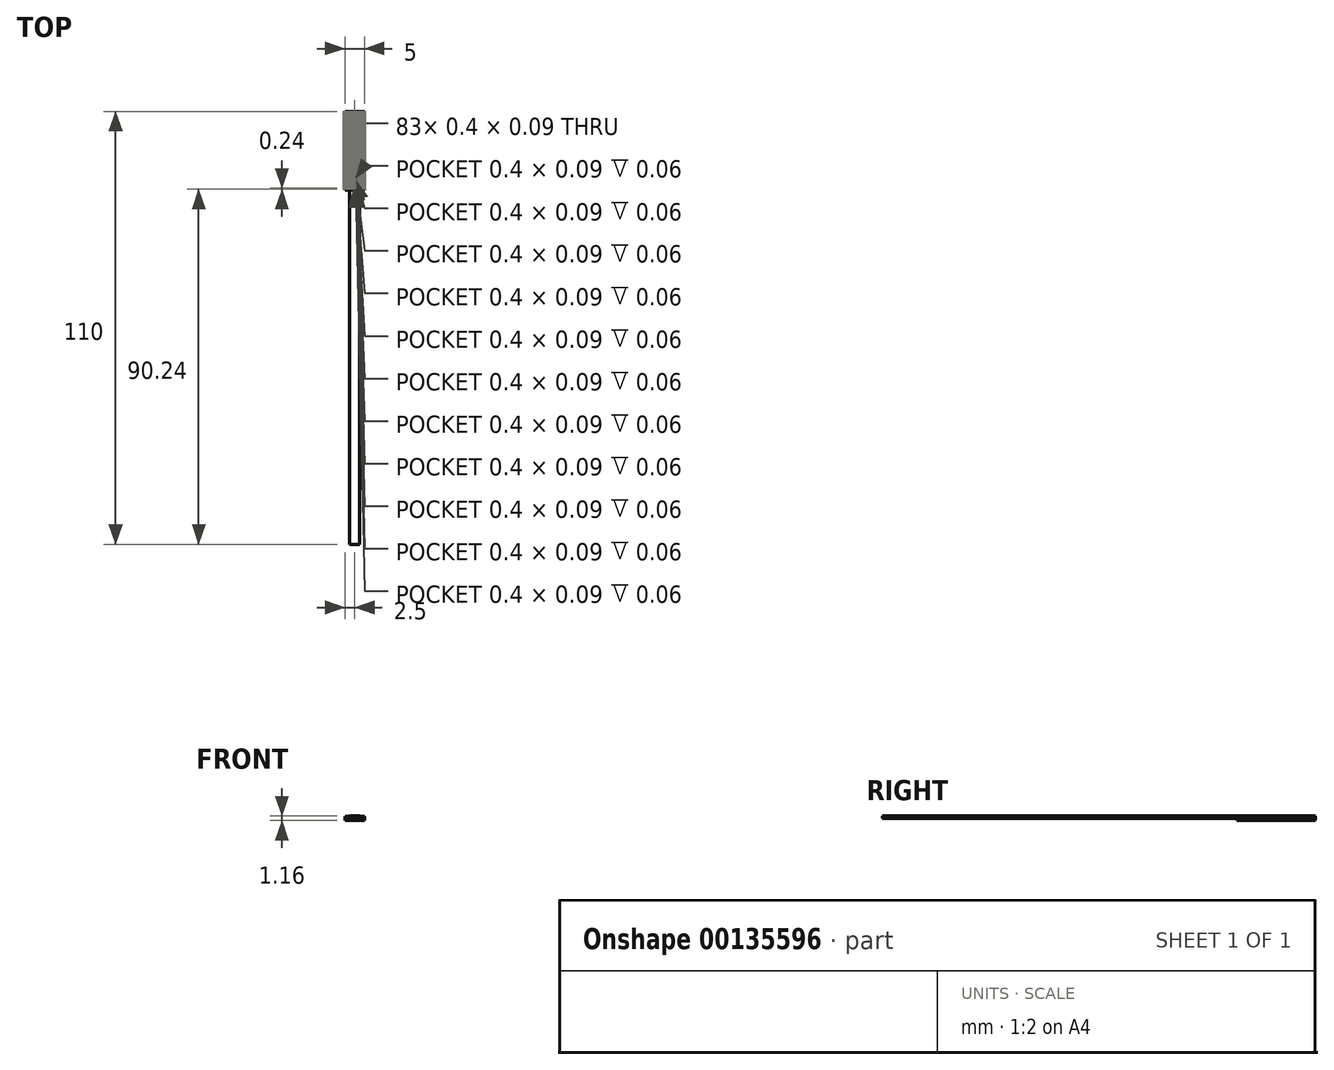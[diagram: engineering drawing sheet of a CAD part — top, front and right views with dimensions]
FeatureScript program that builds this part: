
annotation { "Feature Type Name" : "Feature", "Feature Type Description" : "" }
export const myFeature = defineFeature(function(context is Context, id is Id, definition is map)
    precondition{}
    {
        {
            assignVariable(context, id + "F0", {"name" : "Lz", "anyValue" : 20 * mm});
        }
        {
            var Q0;
            Q0=qCreatedBy(makeId("Top.planeOp"),FACE);
            var sketch = newSketch(context, id + "F1", { "sketchPlane" : qUnion([Q0])});
            skLineSegment(sketch, "E0.bottom", {"start": v(1.25, 10) * mm, "end": v(-1.25, 10) * mm});
            skLineSegment(sketch, "E0.top", {"start": v(1.25, -10) * mm, "end": v(-1.25, -10) * mm});
            skLineSegment(sketch, "E0.left", {"start": v(1.25, 10) * mm, "end": v(1.25, -10) * mm});
            skLineSegment(sketch, "E0.right", {"start": v(-1.25, 10) * mm, "end": v(-1.25, -10) * mm});
            skPoint(sketch, "E0.middle", {"position": v(0, 0) * mm});
            skLineSegment(sketch, "E1.bottom", {"start": v(2.5, 10) * mm, "end": v(-2.5, 10) * mm});
            skLineSegment(sketch, "E1.top", {"start": v(2.5, -10) * mm, "end": v(-2.5, -10) * mm});
            skLineSegment(sketch, "E1.left", {"start": v(2.5, 10) * mm, "end": v(2.5, -10) * mm});
            skLineSegment(sketch, "E1.right", {"start": v(-2.5, 10) * mm, "end": v(-2.5, -10) * mm});
            skSolve(sketch);
        }
        {
            var Q0;
            Q0=qCreatedBy(makeId("Front.planeOp"),FACE);
            var sketch = newSketch(context, id + "F2", { "sketchPlane" : qUnion([Q0])});
            skPoint(sketch, "E2", {"position": v(0.06, -0.1) * mm});
            skEllipse(sketch, "E3", {"center": v(0, -0.17) * mm, "majorRadius": 1.28 * mm, "minorRadius": 0.29 * mm, "majorAxis": v(-1, 0)});
            skSolve(sketch);
        }
        {
            var Q0;
            Q0=makeQuery(id+"F2.imprint","IMPRINT",FACE,{"disambiguationData":[TD([[makeQuery(id+"F2.imprint","IMPRINT",EDGE,{"derivedFrom":sQuery(id+"F2.wireOp",EDGE,"E3")}),1.0]])]});
            extrude(context, id + "F3", {"entities" : qUnion([Q0]), "depth" : 100 * mm, "offsetDistance" : 25 * mm, "hasSecondDirection" : true, "secondDirectionOppositeDirection" : false, "secondDirectionDepth" : getVariable(context, 'Lz') / 2});
        }
        {
            assignVariable(context, id + "F4", {"name" : "tox", "anyValue" : 0.1});
        }
        {
            assignVariable(context, id + "F5", {"name" : "detch", "anyValue" : 0.06});
        }
        {
            assignVariable(context, id + "F6", {"name" : "Hsi", "anyValue" : 0.5});
        }
        {
            var Q0;
            {var subQ0=sQuery(id+"F1.wireOp",EDGE,"E0.right");Q0=makeQuery(id+"F1.imprint","IMPRINT",FACE,{"disambiguationData":[TD([[makeQuery(id+"F1.imprint","IMPRINT",EDGE,{"derivedFrom":subQ0}),-1.0]])]});}
            var Q1;
            {var subQ0=sQuery(id+"F1.wireOp",EDGE,"E0.left");Q1=makeQuery(id+"F1.imprint","IMPRINT",FACE,{"disambiguationData":[TD([[makeQuery(id+"F1.imprint","IMPRINT",EDGE,{"derivedFrom":subQ0}),-1.0]])]});}
            var Q2;
            {var subQ0=sQuery(id+"F1.wireOp",EDGE,"E0.left");Q2=makeQuery(id+"F1.imprint","IMPRINT",FACE,{"disambiguationData":[TD([[makeQuery(id+"F1.imprint","IMPRINT",EDGE,{"derivedFrom":subQ0}),1.0]])]});}
            extrude(context, id + "F7", {"entities" : qUnion([Q0, Q1, Q2]), "oppositeDirection" : true, "depth" : (getVariable(context, 'Hsi') - getVariable(context, 'detch')) * mm});
        }
        {
            var Q0;
            Q0=makeQuery(id+"F7.opExtrude","CAP_FACE",FACE,{"disambiguationData":[OSD([sQuery(id+"F1.wireOp",EDGE,"E1.bottom"),sQuery(id+"F1.wireOp",EDGE,"E1.top"),sQuery(id+"F1.wireOp",EDGE,"E1.left"),sQuery(id+"F1.wireOp",EDGE,"E1.right")])],"isStart":true});
            extrude(context, id + "F8", {"entities" : qUnion([Q0]), "oppositeDirection" : true, "depth" : 1 * mm, "hasSecondDirection" : true, "secondDirectionOppositeDirection" : true, "secondDirectionDepth" : (getVariable(context, 'Hsi') - getVariable(context, 'detch')) * mm});
        }
        {
            var Q0;
            Q0=qCreatedBy(makeId("Top.planeOp"),FACE);
            var sketch = newSketch(context, id + "F9", { "sketchPlane" : qUnion([Q0])});
            skLineSegment(sketch, "E4.bottom", {"start": v(-1.25, 10) * mm, "end": v(1.25, 10) * mm});
            skLineSegment(sketch, "E4.top", {"start": v(-1.25, -10) * mm, "end": v(1.25, -10) * mm});
            skLineSegment(sketch, "E4.left", {"start": v(-1.25, 10) * mm, "end": v(-1.25, -10) * mm});
            skLineSegment(sketch, "E4.right", {"start": v(1.25, 10) * mm, "end": v(1.25, -10) * mm});
            skPoint(sketch, "E4.middle", {"position": v(0, 0) * mm});
            skSolve(sketch);
        }
        {
            var Q0;
            Q0=makeQuery(id+"F9.imprint","IMPRINT",FACE,{"disambiguationData":[TD([[makeQuery(id+"F9.imprint","IMPRINT",EDGE,{"derivedFrom":sQuery(id+"F9.wireOp",EDGE,"E4.bottom")}),-1.0]])]});
            extrude(context, id + "F10", {"entities" : qUnion([Q0]), "operationType" : NewBodyOperationType.ADD, "depth" : (getVariable(context, 'detch')) * mm});
        }
        {
            var Q0;
            Q0=makeQuery(id+"F10.opExtrude","CAP_FACE",FACE,{"disambiguationData":[OSD([sQuery(id+"F9.wireOp",EDGE,"E4.bottom"),sQuery(id+"F9.wireOp",EDGE,"E4.top"),sQuery(id+"F9.wireOp",EDGE,"E4.left"),sQuery(id+"F9.wireOp",EDGE,"E4.right")])],"isStart":false});
            extrude(context, id + "F11", {"entities" : qUnion([Q0]), "depth" : (getVariable(context, 'tox')) * mm});
        }
        {
            var Q0;
            Q0=makeQuery(id+"F11.opExtrude","CAP_FACE",FACE,{"disambiguationData":[OSD([sQuery(id+"F9.wireOp",EDGE,"E4.bottom"),sQuery(id+"F9.wireOp",EDGE,"E4.top"),sQuery(id+"F9.wireOp",EDGE,"E4.left"),sQuery(id+"F9.wireOp",EDGE,"E4.right")])],"isStart":false});
            var sketch = newSketch(context, id + "F12", { "sketchPlane" : qUnion([Q0])});
            skLineSegment(sketch, "E5.bottom", {"start": v(0.2, -9.96) * mm, "end": v(-0.2, -9.96) * mm});
            skLineSegment(sketch, "E5.top", {"start": v(0.2, -10.04) * mm, "end": v(-0.2, -10.04) * mm});
            skLineSegment(sketch, "E5.left", {"start": v(0.2, -9.96) * mm, "end": v(0.2, -10.05) * mm});
            skLineSegment(sketch, "E5.right", {"start": v(-0.2, -9.96) * mm, "end": v(-0.2, -10.05) * mm});
            skPoint(sketch, "E5.middle", {"position": v(0, -10) * mm});
            skLineSegment(sketch, "E6.0.1.0", {"start": v(0.2, -9.72) * mm, "end": v(0.2, -9.8) * mm});
            skLineSegment(sketch, "E6.0.1.1", {"start": v(0.2, -9.8) * mm, "end": v(-0.2, -9.8) * mm});
            skLineSegment(sketch, "E6.0.1.2", {"start": v(-0.2, -9.72) * mm, "end": v(-0.2, -9.8) * mm});
            skLineSegment(sketch, "E6.0.1.3", {"start": v(0.2, -9.72) * mm, "end": v(-0.2, -9.72) * mm});
            skPoint(sketch, "E6.0.1.4", {"position": v(0, -9.76) * mm});
            skLineSegment(sketch, "E6.0.2.0", {"start": v(0.2, -9.48) * mm, "end": v(0.2, -9.57) * mm});
            skLineSegment(sketch, "E6.0.2.1", {"start": v(0.2, -9.56) * mm, "end": v(-0.2, -9.56) * mm});
            skLineSegment(sketch, "E6.0.2.2", {"start": v(-0.2, -9.48) * mm, "end": v(-0.2, -9.57) * mm});
            skLineSegment(sketch, "E6.0.2.3", {"start": v(0.2, -9.48) * mm, "end": v(-0.2, -9.48) * mm});
            skPoint(sketch, "E6.0.2.4", {"position": v(0, -9.52) * mm});
            skLineSegment(sketch, "E6.0.3.0", {"start": v(0.2, -9.24) * mm, "end": v(0.2, -9.33) * mm});
            skLineSegment(sketch, "E6.0.3.1", {"start": v(0.2, -9.32) * mm, "end": v(-0.2, -9.32) * mm});
            skLineSegment(sketch, "E6.0.3.2", {"start": v(-0.2, -9.24) * mm, "end": v(-0.2, -9.33) * mm});
            skLineSegment(sketch, "E6.0.3.3", {"start": v(0.2, -9.24) * mm, "end": v(-0.2, -9.24) * mm});
            skPoint(sketch, "E6.0.3.4", {"position": v(0, -9.28) * mm});
            skLineSegment(sketch, "E6.0.4.0", {"start": v(0.2, -9) * mm, "end": v(0.2, -9.09) * mm});
            skLineSegment(sketch, "E6.0.4.1", {"start": v(0.2, -9.08) * mm, "end": v(-0.2, -9.08) * mm});
            skLineSegment(sketch, "E6.0.4.2", {"start": v(-0.2, -9) * mm, "end": v(-0.2, -9.09) * mm});
            skLineSegment(sketch, "E6.0.4.3", {"start": v(0.2, -9) * mm, "end": v(-0.2, -9) * mm});
            skPoint(sketch, "E6.0.4.4", {"position": v(0, -9.04) * mm});
            skLineSegment(sketch, "E6.0.5.0", {"start": v(0.2, -8.76) * mm, "end": v(0.2, -8.85) * mm});
            skLineSegment(sketch, "E6.0.5.1", {"start": v(0.2, -8.84) * mm, "end": v(-0.2, -8.84) * mm});
            skLineSegment(sketch, "E6.0.5.2", {"start": v(-0.2, -8.76) * mm, "end": v(-0.2, -8.85) * mm});
            skLineSegment(sketch, "E6.0.5.3", {"start": v(0.2, -8.76) * mm, "end": v(-0.2, -8.76) * mm});
            skPoint(sketch, "E6.0.5.4", {"position": v(0, -8.8) * mm});
            skLineSegment(sketch, "E6.0.6.0", {"start": v(0.2, -8.52) * mm, "end": v(0.2, -8.6) * mm});
            skLineSegment(sketch, "E6.0.6.1", {"start": v(0.2, -8.6) * mm, "end": v(-0.2, -8.6) * mm});
            skLineSegment(sketch, "E6.0.6.2", {"start": v(-0.2, -8.52) * mm, "end": v(-0.2, -8.6) * mm});
            skLineSegment(sketch, "E6.0.6.3", {"start": v(0.2, -8.52) * mm, "end": v(-0.2, -8.52) * mm});
            skPoint(sketch, "E6.0.6.4", {"position": v(0, -8.56) * mm});
            skLineSegment(sketch, "E6.0.7.0", {"start": v(0.2, -8.28) * mm, "end": v(0.2, -8.37) * mm});
            skLineSegment(sketch, "E6.0.7.1", {"start": v(0.2, -8.36) * mm, "end": v(-0.2, -8.36) * mm});
            skLineSegment(sketch, "E6.0.7.2", {"start": v(-0.2, -8.28) * mm, "end": v(-0.2, -8.37) * mm});
            skLineSegment(sketch, "E6.0.7.3", {"start": v(0.2, -8.28) * mm, "end": v(-0.2, -8.28) * mm});
            skPoint(sketch, "E6.0.7.4", {"position": v(0, -8.32) * mm});
            skLineSegment(sketch, "E6.0.8.0", {"start": v(0.2, -8.04) * mm, "end": v(0.2, -8.13) * mm});
            skLineSegment(sketch, "E6.0.8.1", {"start": v(0.2, -8.12) * mm, "end": v(-0.2, -8.12) * mm});
            skLineSegment(sketch, "E6.0.8.2", {"start": v(-0.2, -8.04) * mm, "end": v(-0.2, -8.13) * mm});
            skLineSegment(sketch, "E6.0.8.3", {"start": v(0.2, -8.04) * mm, "end": v(-0.2, -8.04) * mm});
            skPoint(sketch, "E6.0.8.4", {"position": v(0, -8.08) * mm});
            skLineSegment(sketch, "E6.0.9.0", {"start": v(0.2, -7.8) * mm, "end": v(0.2, -7.89) * mm});
            skLineSegment(sketch, "E6.0.9.1", {"start": v(0.2, -7.88) * mm, "end": v(-0.2, -7.88) * mm});
            skLineSegment(sketch, "E6.0.9.2", {"start": v(-0.2, -7.8) * mm, "end": v(-0.2, -7.89) * mm});
            skLineSegment(sketch, "E6.0.9.3", {"start": v(0.2, -7.8) * mm, "end": v(-0.2, -7.8) * mm});
            skPoint(sketch, "E6.0.9.4", {"position": v(0, -7.84) * mm});
            skLineSegment(sketch, "E6.direction1", {"start": v(-0.2, -10.04) * mm, "end": v(24.8, -10.04) * mm, "construction": true});
            skLineSegment(sketch, "E6.direction2", {"start": v(-0.2, -10.05) * mm, "end": v(-0.2, -9.8) * mm, "construction": true});
            skLineSegment(sketch, "E7.0.0.10", {"start": v(0.2, -7.56) * mm, "end": v(0.2, -7.65) * mm});
            skLineSegment(sketch, "E7.3.0.10", {"start": v(0.2, -7.64) * mm, "end": v(-0.2, -7.64) * mm});
            skLineSegment(sketch, "E7.6.0.10", {"start": v(-0.2, -7.56) * mm, "end": v(-0.2, -7.65) * mm});
            skLineSegment(sketch, "E7.9.0.10", {"start": v(0.2, -7.56) * mm, "end": v(-0.2, -7.56) * mm});
            skPoint(sketch, "E7.12.0.10", {"position": v(0, -7.6) * mm});
            skLineSegment(sketch, "E7.0.0.11", {"start": v(0.2, -7.32) * mm, "end": v(0.2, -7.4) * mm});
            skLineSegment(sketch, "E7.3.0.11", {"start": v(0.2, -7.4) * mm, "end": v(-0.2, -7.4) * mm});
            skLineSegment(sketch, "E7.6.0.11", {"start": v(-0.2, -7.32) * mm, "end": v(-0.2, -7.4) * mm});
            skLineSegment(sketch, "E7.9.0.11", {"start": v(0.2, -7.32) * mm, "end": v(-0.2, -7.32) * mm});
            skPoint(sketch, "E7.12.0.11", {"position": v(0, -7.36) * mm});
            skLineSegment(sketch, "E7.0.0.12", {"start": v(0.2, -7.08) * mm, "end": v(0.2, -7.17) * mm});
            skLineSegment(sketch, "E7.3.0.12", {"start": v(0.2, -7.16) * mm, "end": v(-0.2, -7.16) * mm});
            skLineSegment(sketch, "E7.6.0.12", {"start": v(-0.2, -7.08) * mm, "end": v(-0.2, -7.17) * mm});
            skLineSegment(sketch, "E7.9.0.12", {"start": v(0.2, -7.08) * mm, "end": v(-0.2, -7.08) * mm});
            skPoint(sketch, "E7.12.0.12", {"position": v(0, -7.12) * mm});
            skLineSegment(sketch, "E7.0.0.13", {"start": v(0.2, -6.84) * mm, "end": v(0.2, -6.93) * mm});
            skLineSegment(sketch, "E7.3.0.13", {"start": v(0.2, -6.92) * mm, "end": v(-0.2, -6.92) * mm});
            skLineSegment(sketch, "E7.6.0.13", {"start": v(-0.2, -6.84) * mm, "end": v(-0.2, -6.93) * mm});
            skLineSegment(sketch, "E7.9.0.13", {"start": v(0.2, -6.84) * mm, "end": v(-0.2, -6.84) * mm});
            skPoint(sketch, "E7.12.0.13", {"position": v(0, -6.88) * mm});
            skLineSegment(sketch, "E7.0.0.14", {"start": v(0.2, -6.6) * mm, "end": v(0.2, -6.69) * mm});
            skLineSegment(sketch, "E7.3.0.14", {"start": v(0.2, -6.68) * mm, "end": v(-0.2, -6.68) * mm});
            skLineSegment(sketch, "E7.6.0.14", {"start": v(-0.2, -6.6) * mm, "end": v(-0.2, -6.69) * mm});
            skLineSegment(sketch, "E7.9.0.14", {"start": v(0.2, -6.6) * mm, "end": v(-0.2, -6.6) * mm});
            skPoint(sketch, "E7.12.0.14", {"position": v(0, -6.64) * mm});
            skLineSegment(sketch, "E7.0.0.15", {"start": v(0.2, -6.36) * mm, "end": v(0.2, -6.45) * mm});
            skLineSegment(sketch, "E7.3.0.15", {"start": v(0.2, -6.44) * mm, "end": v(-0.2, -6.44) * mm});
            skLineSegment(sketch, "E7.6.0.15", {"start": v(-0.2, -6.36) * mm, "end": v(-0.2, -6.45) * mm});
            skLineSegment(sketch, "E7.9.0.15", {"start": v(0.2, -6.36) * mm, "end": v(-0.2, -6.36) * mm});
            skPoint(sketch, "E7.12.0.15", {"position": v(0, -6.4) * mm});
            skLineSegment(sketch, "E7.0.0.16", {"start": v(0.2, -6.12) * mm, "end": v(0.2, -6.2) * mm});
            skLineSegment(sketch, "E7.3.0.16", {"start": v(0.2, -6.2) * mm, "end": v(-0.2, -6.2) * mm});
            skLineSegment(sketch, "E7.6.0.16", {"start": v(-0.2, -6.12) * mm, "end": v(-0.2, -6.2) * mm});
            skLineSegment(sketch, "E7.9.0.16", {"start": v(0.2, -6.12) * mm, "end": v(-0.2, -6.12) * mm});
            skPoint(sketch, "E7.12.0.16", {"position": v(0, -6.16) * mm});
            skLineSegment(sketch, "E7.0.0.17", {"start": v(0.2, -5.88) * mm, "end": v(0.2, -5.97) * mm});
            skLineSegment(sketch, "E7.3.0.17", {"start": v(0.2, -5.96) * mm, "end": v(-0.2, -5.96) * mm});
            skLineSegment(sketch, "E7.6.0.17", {"start": v(-0.2, -5.88) * mm, "end": v(-0.2, -5.97) * mm});
            skLineSegment(sketch, "E7.9.0.17", {"start": v(0.2, -5.88) * mm, "end": v(-0.2, -5.88) * mm});
            skPoint(sketch, "E7.12.0.17", {"position": v(0, -5.92) * mm});
            skLineSegment(sketch, "E7.0.0.18", {"start": v(0.2, -5.64) * mm, "end": v(0.2, -5.73) * mm});
            skLineSegment(sketch, "E7.3.0.18", {"start": v(0.2, -5.72) * mm, "end": v(-0.2, -5.72) * mm});
            skLineSegment(sketch, "E7.6.0.18", {"start": v(-0.2, -5.64) * mm, "end": v(-0.2, -5.73) * mm});
            skLineSegment(sketch, "E7.9.0.18", {"start": v(0.2, -5.64) * mm, "end": v(-0.2, -5.64) * mm});
            skPoint(sketch, "E7.12.0.18", {"position": v(0, -5.68) * mm});
            skLineSegment(sketch, "E7.0.0.19", {"start": v(0.2, -5.4) * mm, "end": v(0.2, -5.49) * mm});
            skLineSegment(sketch, "E7.3.0.19", {"start": v(0.2, -5.48) * mm, "end": v(-0.2, -5.48) * mm});
            skLineSegment(sketch, "E7.6.0.19", {"start": v(-0.2, -5.4) * mm, "end": v(-0.2, -5.49) * mm});
            skLineSegment(sketch, "E7.9.0.19", {"start": v(0.2, -5.4) * mm, "end": v(-0.2, -5.4) * mm});
            skPoint(sketch, "E7.12.0.19", {"position": v(0, -5.44) * mm});
            skLineSegment(sketch, "E7.0.0.20", {"start": v(0.2, -5.16) * mm, "end": v(0.2, -5.25) * mm});
            skLineSegment(sketch, "E7.3.0.20", {"start": v(0.2, -5.24) * mm, "end": v(-0.2, -5.24) * mm});
            skLineSegment(sketch, "E7.6.0.20", {"start": v(-0.2, -5.16) * mm, "end": v(-0.2, -5.25) * mm});
            skLineSegment(sketch, "E7.9.0.20", {"start": v(0.2, -5.16) * mm, "end": v(-0.2, -5.16) * mm});
            skPoint(sketch, "E7.12.0.20", {"position": v(0, -5.2) * mm});
            skLineSegment(sketch, "E7.0.0.21", {"start": v(0.2, -4.92) * mm, "end": v(0.2, -5) * mm});
            skLineSegment(sketch, "E7.3.0.21", {"start": v(0.2, -5) * mm, "end": v(-0.2, -5) * mm});
            skLineSegment(sketch, "E7.6.0.21", {"start": v(-0.2, -4.92) * mm, "end": v(-0.2, -5) * mm});
            skLineSegment(sketch, "E7.9.0.21", {"start": v(0.2, -4.92) * mm, "end": v(-0.2, -4.92) * mm});
            skPoint(sketch, "E7.12.0.21", {"position": v(0, -4.96) * mm});
            skLineSegment(sketch, "E7.0.0.22", {"start": v(0.2, -4.68) * mm, "end": v(0.2, -4.77) * mm});
            skLineSegment(sketch, "E7.3.0.22", {"start": v(0.2, -4.76) * mm, "end": v(-0.2, -4.76) * mm});
            skLineSegment(sketch, "E7.6.0.22", {"start": v(-0.2, -4.68) * mm, "end": v(-0.2, -4.77) * mm});
            skLineSegment(sketch, "E7.9.0.22", {"start": v(0.2, -4.68) * mm, "end": v(-0.2, -4.68) * mm});
            skPoint(sketch, "E7.12.0.22", {"position": v(0, -4.72) * mm});
            skLineSegment(sketch, "E7.0.0.23", {"start": v(0.2, -4.44) * mm, "end": v(0.2, -4.53) * mm});
            skLineSegment(sketch, "E7.3.0.23", {"start": v(0.2, -4.52) * mm, "end": v(-0.2, -4.52) * mm});
            skLineSegment(sketch, "E7.6.0.23", {"start": v(-0.2, -4.44) * mm, "end": v(-0.2, -4.53) * mm});
            skLineSegment(sketch, "E7.9.0.23", {"start": v(0.2, -4.44) * mm, "end": v(-0.2, -4.44) * mm});
            skPoint(sketch, "E7.12.0.23", {"position": v(0, -4.48) * mm});
            skLineSegment(sketch, "E7.0.0.24", {"start": v(0.2, -4.2) * mm, "end": v(0.2, -4.29) * mm});
            skLineSegment(sketch, "E7.3.0.24", {"start": v(0.2, -4.28) * mm, "end": v(-0.2, -4.28) * mm});
            skLineSegment(sketch, "E7.6.0.24", {"start": v(-0.2, -4.2) * mm, "end": v(-0.2, -4.29) * mm});
            skLineSegment(sketch, "E7.9.0.24", {"start": v(0.2, -4.2) * mm, "end": v(-0.2, -4.2) * mm});
            skPoint(sketch, "E7.12.0.24", {"position": v(0, -4.24) * mm});
            skLineSegment(sketch, "E7.0.0.25", {"start": v(0.2, -3.96) * mm, "end": v(0.2, -4.05) * mm});
            skLineSegment(sketch, "E7.3.0.25", {"start": v(0.2, -4.04) * mm, "end": v(-0.2, -4.04) * mm});
            skLineSegment(sketch, "E7.6.0.25", {"start": v(-0.2, -3.96) * mm, "end": v(-0.2, -4.05) * mm});
            skLineSegment(sketch, "E7.9.0.25", {"start": v(0.2, -3.96) * mm, "end": v(-0.2, -3.96) * mm});
            skPoint(sketch, "E7.12.0.25", {"position": v(0, -4) * mm});
            skLineSegment(sketch, "E7.0.0.26", {"start": v(0.2, -3.72) * mm, "end": v(0.2, -3.8) * mm});
            skLineSegment(sketch, "E7.3.0.26", {"start": v(0.2, -3.8) * mm, "end": v(-0.2, -3.8) * mm});
            skLineSegment(sketch, "E7.6.0.26", {"start": v(-0.2, -3.72) * mm, "end": v(-0.2, -3.8) * mm});
            skLineSegment(sketch, "E7.9.0.26", {"start": v(0.2, -3.72) * mm, "end": v(-0.2, -3.72) * mm});
            skPoint(sketch, "E7.12.0.26", {"position": v(0, -3.76) * mm});
            skLineSegment(sketch, "E7.0.0.27", {"start": v(0.2, -3.48) * mm, "end": v(0.2, -3.57) * mm});
            skLineSegment(sketch, "E7.3.0.27", {"start": v(0.2, -3.56) * mm, "end": v(-0.2, -3.56) * mm});
            skLineSegment(sketch, "E7.6.0.27", {"start": v(-0.2, -3.48) * mm, "end": v(-0.2, -3.57) * mm});
            skLineSegment(sketch, "E7.9.0.27", {"start": v(0.2, -3.48) * mm, "end": v(-0.2, -3.48) * mm});
            skPoint(sketch, "E7.12.0.27", {"position": v(0, -3.52) * mm});
            skLineSegment(sketch, "E7.0.0.28", {"start": v(0.2, -3.24) * mm, "end": v(0.2, -3.33) * mm});
            skLineSegment(sketch, "E7.3.0.28", {"start": v(0.2, -3.32) * mm, "end": v(-0.2, -3.32) * mm});
            skLineSegment(sketch, "E7.6.0.28", {"start": v(-0.2, -3.24) * mm, "end": v(-0.2, -3.33) * mm});
            skLineSegment(sketch, "E7.9.0.28", {"start": v(0.2, -3.24) * mm, "end": v(-0.2, -3.24) * mm});
            skPoint(sketch, "E7.12.0.28", {"position": v(0, -3.28) * mm});
            skLineSegment(sketch, "E7.0.0.29", {"start": v(0.2, -3) * mm, "end": v(0.2, -3.09) * mm});
            skLineSegment(sketch, "E7.3.0.29", {"start": v(0.2, -3.08) * mm, "end": v(-0.2, -3.08) * mm});
            skLineSegment(sketch, "E7.6.0.29", {"start": v(-0.2, -3) * mm, "end": v(-0.2, -3.09) * mm});
            skLineSegment(sketch, "E7.9.0.29", {"start": v(0.2, -3) * mm, "end": v(-0.2, -3) * mm});
            skPoint(sketch, "E7.12.0.29", {"position": v(0, -3.04) * mm});
            skLineSegment(sketch, "E7.0.0.30", {"start": v(0.2, -2.76) * mm, "end": v(0.2, -2.85) * mm});
            skLineSegment(sketch, "E7.3.0.30", {"start": v(0.2, -2.84) * mm, "end": v(-0.2, -2.84) * mm});
            skLineSegment(sketch, "E7.6.0.30", {"start": v(-0.2, -2.76) * mm, "end": v(-0.2, -2.85) * mm});
            skLineSegment(sketch, "E7.9.0.30", {"start": v(0.2, -2.76) * mm, "end": v(-0.2, -2.76) * mm});
            skPoint(sketch, "E7.12.0.30", {"position": v(0, -2.8) * mm});
            skLineSegment(sketch, "E7.0.0.31", {"start": v(0.2, -2.52) * mm, "end": v(0.2, -2.6) * mm});
            skLineSegment(sketch, "E7.3.0.31", {"start": v(0.2, -2.6) * mm, "end": v(-0.2, -2.6) * mm});
            skLineSegment(sketch, "E7.6.0.31", {"start": v(-0.2, -2.52) * mm, "end": v(-0.2, -2.6) * mm});
            skLineSegment(sketch, "E7.9.0.31", {"start": v(0.2, -2.52) * mm, "end": v(-0.2, -2.52) * mm});
            skPoint(sketch, "E7.12.0.31", {"position": v(0, -2.56) * mm});
            skLineSegment(sketch, "E7.0.0.32", {"start": v(0.2, -2.28) * mm, "end": v(0.2, -2.37) * mm});
            skLineSegment(sketch, "E7.3.0.32", {"start": v(0.2, -2.36) * mm, "end": v(-0.2, -2.36) * mm});
            skLineSegment(sketch, "E7.6.0.32", {"start": v(-0.2, -2.28) * mm, "end": v(-0.2, -2.37) * mm});
            skLineSegment(sketch, "E7.9.0.32", {"start": v(0.2, -2.28) * mm, "end": v(-0.2, -2.28) * mm});
            skPoint(sketch, "E7.12.0.32", {"position": v(0, -2.32) * mm});
            skLineSegment(sketch, "E7.0.0.33", {"start": v(0.2, -2.04) * mm, "end": v(0.2, -2.13) * mm});
            skLineSegment(sketch, "E7.3.0.33", {"start": v(0.2, -2.12) * mm, "end": v(-0.2, -2.12) * mm});
            skLineSegment(sketch, "E7.6.0.33", {"start": v(-0.2, -2.04) * mm, "end": v(-0.2, -2.13) * mm});
            skLineSegment(sketch, "E7.9.0.33", {"start": v(0.2, -2.04) * mm, "end": v(-0.2, -2.04) * mm});
            skPoint(sketch, "E7.12.0.33", {"position": v(0, -2.08) * mm});
            skLineSegment(sketch, "E7.0.0.34", {"start": v(0.2, -1.8) * mm, "end": v(0.2, -1.89) * mm});
            skLineSegment(sketch, "E7.3.0.34", {"start": v(0.2, -1.88) * mm, "end": v(-0.2, -1.88) * mm});
            skLineSegment(sketch, "E7.6.0.34", {"start": v(-0.2, -1.8) * mm, "end": v(-0.2, -1.89) * mm});
            skLineSegment(sketch, "E7.9.0.34", {"start": v(0.2, -1.8) * mm, "end": v(-0.2, -1.8) * mm});
            skPoint(sketch, "E7.12.0.34", {"position": v(0, -1.84) * mm});
            skLineSegment(sketch, "E7.0.0.35", {"start": v(0.2, -1.56) * mm, "end": v(0.2, -1.65) * mm});
            skLineSegment(sketch, "E7.3.0.35", {"start": v(0.2, -1.64) * mm, "end": v(-0.2, -1.64) * mm});
            skLineSegment(sketch, "E7.6.0.35", {"start": v(-0.2, -1.56) * mm, "end": v(-0.2, -1.65) * mm});
            skLineSegment(sketch, "E7.9.0.35", {"start": v(0.2, -1.56) * mm, "end": v(-0.2, -1.56) * mm});
            skPoint(sketch, "E7.12.0.35", {"position": v(0, -1.6) * mm});
            skLineSegment(sketch, "E7.0.0.36", {"start": v(0.2, -1.32) * mm, "end": v(0.2, -1.4) * mm});
            skLineSegment(sketch, "E7.3.0.36", {"start": v(0.2, -1.4) * mm, "end": v(-0.2, -1.4) * mm});
            skLineSegment(sketch, "E7.6.0.36", {"start": v(-0.2, -1.32) * mm, "end": v(-0.2, -1.4) * mm});
            skLineSegment(sketch, "E7.9.0.36", {"start": v(0.2, -1.32) * mm, "end": v(-0.2, -1.32) * mm});
            skPoint(sketch, "E7.12.0.36", {"position": v(0, -1.36) * mm});
            skLineSegment(sketch, "E7.0.0.37", {"start": v(0.2, -1.08) * mm, "end": v(0.2, -1.17) * mm});
            skLineSegment(sketch, "E7.3.0.37", {"start": v(0.2, -1.16) * mm, "end": v(-0.2, -1.16) * mm});
            skLineSegment(sketch, "E7.6.0.37", {"start": v(-0.2, -1.08) * mm, "end": v(-0.2, -1.17) * mm});
            skLineSegment(sketch, "E7.9.0.37", {"start": v(0.2, -1.08) * mm, "end": v(-0.2, -1.08) * mm});
            skPoint(sketch, "E7.12.0.37", {"position": v(0, -1.12) * mm});
            skLineSegment(sketch, "E7.0.0.38", {"start": v(0.2, -0.84) * mm, "end": v(0.2, -0.93) * mm});
            skLineSegment(sketch, "E7.3.0.38", {"start": v(0.2, -0.92) * mm, "end": v(-0.2, -0.92) * mm});
            skLineSegment(sketch, "E7.6.0.38", {"start": v(-0.2, -0.84) * mm, "end": v(-0.2, -0.93) * mm});
            skLineSegment(sketch, "E7.9.0.38", {"start": v(0.2, -0.84) * mm, "end": v(-0.2, -0.84) * mm});
            skPoint(sketch, "E7.12.0.38", {"position": v(0, -0.88) * mm});
            skLineSegment(sketch, "E7.0.0.39", {"start": v(0.2, -0.6) * mm, "end": v(0.2, -0.69) * mm});
            skLineSegment(sketch, "E7.3.0.39", {"start": v(0.2, -0.68) * mm, "end": v(-0.2, -0.68) * mm});
            skLineSegment(sketch, "E7.6.0.39", {"start": v(-0.2, -0.6) * mm, "end": v(-0.2, -0.69) * mm});
            skLineSegment(sketch, "E7.9.0.39", {"start": v(0.2, -0.6) * mm, "end": v(-0.2, -0.6) * mm});
            skPoint(sketch, "E7.12.0.39", {"position": v(0, -0.64) * mm});
            skLineSegment(sketch, "E7.0.0.40", {"start": v(0.2, -0.36) * mm, "end": v(0.2, -0.45) * mm});
            skLineSegment(sketch, "E7.3.0.40", {"start": v(0.2, -0.44) * mm, "end": v(-0.2, -0.44) * mm});
            skLineSegment(sketch, "E7.6.0.40", {"start": v(-0.2, -0.36) * mm, "end": v(-0.2, -0.45) * mm});
            skLineSegment(sketch, "E7.9.0.40", {"start": v(0.2, -0.36) * mm, "end": v(-0.2, -0.36) * mm});
            skPoint(sketch, "E7.12.0.40", {"position": v(0, -0.4) * mm});
            skLineSegment(sketch, "E7.0.0.41", {"start": v(0.2, -0.12) * mm, "end": v(0.2, -0.2) * mm});
            skLineSegment(sketch, "E7.3.0.41", {"start": v(0.2, -0.2) * mm, "end": v(-0.2, -0.2) * mm});
            skLineSegment(sketch, "E7.6.0.41", {"start": v(-0.2, -0.12) * mm, "end": v(-0.2, -0.2) * mm});
            skLineSegment(sketch, "E7.9.0.41", {"start": v(0.2, -0.12) * mm, "end": v(-0.2, -0.12) * mm});
            skPoint(sketch, "E7.12.0.41", {"position": v(0, -0.16) * mm});
            skLineSegment(sketch, "E8.0.0.42", {"start": v(0.2, 0.12) * mm, "end": v(0.2, 0.03) * mm});
            skLineSegment(sketch, "E8.3.0.42", {"start": v(0.2, 0.04) * mm, "end": v(-0.2, 0.04) * mm});
            skLineSegment(sketch, "E8.6.0.42", {"start": v(-0.2, 0.12) * mm, "end": v(-0.2, 0.03) * mm});
            skLineSegment(sketch, "E8.9.0.42", {"start": v(0.2, 0.12) * mm, "end": v(-0.2, 0.12) * mm});
            skPoint(sketch, "E8.12.0.42", {"position": v(0, 0.08) * mm});
            skLineSegment(sketch, "E8.0.0.43", {"start": v(0.2, 0.36) * mm, "end": v(0.2, 0.27) * mm});
            skLineSegment(sketch, "E8.3.0.43", {"start": v(0.2, 0.28) * mm, "end": v(-0.2, 0.28) * mm});
            skLineSegment(sketch, "E8.6.0.43", {"start": v(-0.2, 0.36) * mm, "end": v(-0.2, 0.27) * mm});
            skLineSegment(sketch, "E8.9.0.43", {"start": v(0.2, 0.36) * mm, "end": v(-0.2, 0.36) * mm});
            skPoint(sketch, "E8.12.0.43", {"position": v(0, 0.32) * mm});
            skLineSegment(sketch, "E8.0.0.44", {"start": v(0.2, 0.6) * mm, "end": v(0.2, 0.51) * mm});
            skLineSegment(sketch, "E8.3.0.44", {"start": v(0.2, 0.52) * mm, "end": v(-0.2, 0.52) * mm});
            skLineSegment(sketch, "E8.6.0.44", {"start": v(-0.2, 0.6) * mm, "end": v(-0.2, 0.51) * mm});
            skLineSegment(sketch, "E8.9.0.44", {"start": v(0.2, 0.6) * mm, "end": v(-0.2, 0.6) * mm});
            skPoint(sketch, "E8.12.0.44", {"position": v(0, 0.56) * mm});
            skLineSegment(sketch, "E8.0.0.45", {"start": v(0.2, 0.84) * mm, "end": v(0.2, 0.75) * mm});
            skLineSegment(sketch, "E8.3.0.45", {"start": v(0.2, 0.76) * mm, "end": v(-0.2, 0.76) * mm});
            skLineSegment(sketch, "E8.6.0.45", {"start": v(-0.2, 0.84) * mm, "end": v(-0.2, 0.75) * mm});
            skLineSegment(sketch, "E8.9.0.45", {"start": v(0.2, 0.84) * mm, "end": v(-0.2, 0.84) * mm});
            skPoint(sketch, "E8.12.0.45", {"position": v(0, 0.8) * mm});
            skLineSegment(sketch, "E8.0.0.46", {"start": v(0.2, 1.08) * mm, "end": v(0.2, 1) * mm});
            skLineSegment(sketch, "E8.3.0.46", {"start": v(0.2, 1) * mm, "end": v(-0.2, 1) * mm});
            skLineSegment(sketch, "E8.6.0.46", {"start": v(-0.2, 1.08) * mm, "end": v(-0.2, 1) * mm});
            skLineSegment(sketch, "E8.9.0.46", {"start": v(0.2, 1.08) * mm, "end": v(-0.2, 1.08) * mm});
            skPoint(sketch, "E8.12.0.46", {"position": v(0, 1.04) * mm});
            skLineSegment(sketch, "E8.0.0.47", {"start": v(0.2, 1.32) * mm, "end": v(0.2, 1.23) * mm});
            skLineSegment(sketch, "E8.3.0.47", {"start": v(0.2, 1.23) * mm, "end": v(-0.2, 1.23) * mm});
            skLineSegment(sketch, "E8.6.0.47", {"start": v(-0.2, 1.32) * mm, "end": v(-0.2, 1.23) * mm});
            skLineSegment(sketch, "E8.9.0.47", {"start": v(0.2, 1.32) * mm, "end": v(-0.2, 1.32) * mm});
            skPoint(sketch, "E8.12.0.47", {"position": v(0, 1.28) * mm});
            skLineSegment(sketch, "E8.0.0.48", {"start": v(0.2, 1.56) * mm, "end": v(0.2, 1.47) * mm});
            skLineSegment(sketch, "E8.3.0.48", {"start": v(0.2, 1.48) * mm, "end": v(-0.2, 1.48) * mm});
            skLineSegment(sketch, "E8.6.0.48", {"start": v(-0.2, 1.56) * mm, "end": v(-0.2, 1.47) * mm});
            skLineSegment(sketch, "E8.9.0.48", {"start": v(0.2, 1.56) * mm, "end": v(-0.2, 1.56) * mm});
            skPoint(sketch, "E8.12.0.48", {"position": v(0, 1.52) * mm});
            skLineSegment(sketch, "E8.0.0.49", {"start": v(0.2, 1.8) * mm, "end": v(0.2, 1.71) * mm});
            skLineSegment(sketch, "E8.3.0.49", {"start": v(0.2, 1.72) * mm, "end": v(-0.2, 1.72) * mm});
            skLineSegment(sketch, "E8.6.0.49", {"start": v(-0.2, 1.8) * mm, "end": v(-0.2, 1.71) * mm});
            skLineSegment(sketch, "E8.9.0.49", {"start": v(0.2, 1.8) * mm, "end": v(-0.2, 1.8) * mm});
            skPoint(sketch, "E8.12.0.49", {"position": v(0, 1.76) * mm});
            skLineSegment(sketch, "E8.0.0.50", {"start": v(0.2, 2.04) * mm, "end": v(0.2, 1.95) * mm});
            skLineSegment(sketch, "E8.3.0.50", {"start": v(0.2, 1.96) * mm, "end": v(-0.2, 1.96) * mm});
            skLineSegment(sketch, "E8.6.0.50", {"start": v(-0.2, 2.04) * mm, "end": v(-0.2, 1.95) * mm});
            skLineSegment(sketch, "E8.9.0.50", {"start": v(0.2, 2.04) * mm, "end": v(-0.2, 2.04) * mm});
            skPoint(sketch, "E8.12.0.50", {"position": v(0, 2) * mm});
            skLineSegment(sketch, "E8.0.0.51", {"start": v(0.2, 2.28) * mm, "end": v(0.2, 2.2) * mm});
            skLineSegment(sketch, "E8.3.0.51", {"start": v(0.2, 2.2) * mm, "end": v(-0.2, 2.2) * mm});
            skLineSegment(sketch, "E8.6.0.51", {"start": v(-0.2, 2.28) * mm, "end": v(-0.2, 2.2) * mm});
            skLineSegment(sketch, "E8.9.0.51", {"start": v(0.2, 2.28) * mm, "end": v(-0.2, 2.28) * mm});
            skPoint(sketch, "E8.12.0.51", {"position": v(0, 2.24) * mm});
            skLineSegment(sketch, "E8.0.0.52", {"start": v(0.2, 2.52) * mm, "end": v(0.2, 2.43) * mm});
            skLineSegment(sketch, "E8.3.0.52", {"start": v(0.2, 2.44) * mm, "end": v(-0.2, 2.44) * mm});
            skLineSegment(sketch, "E8.6.0.52", {"start": v(-0.2, 2.52) * mm, "end": v(-0.2, 2.43) * mm});
            skLineSegment(sketch, "E8.9.0.52", {"start": v(0.2, 2.52) * mm, "end": v(-0.2, 2.52) * mm});
            skPoint(sketch, "E8.12.0.52", {"position": v(0, 2.48) * mm});
            skLineSegment(sketch, "E8.0.0.53", {"start": v(0.2, 2.76) * mm, "end": v(0.2, 2.67) * mm});
            skLineSegment(sketch, "E8.3.0.53", {"start": v(0.2, 2.68) * mm, "end": v(-0.2, 2.68) * mm});
            skLineSegment(sketch, "E8.6.0.53", {"start": v(-0.2, 2.76) * mm, "end": v(-0.2, 2.67) * mm});
            skLineSegment(sketch, "E8.9.0.53", {"start": v(0.2, 2.76) * mm, "end": v(-0.2, 2.76) * mm});
            skPoint(sketch, "E8.12.0.53", {"position": v(0, 2.72) * mm});
            skLineSegment(sketch, "E8.0.0.54", {"start": v(0.2, 3) * mm, "end": v(0.2, 2.91) * mm});
            skLineSegment(sketch, "E8.3.0.54", {"start": v(0.2, 2.92) * mm, "end": v(-0.2, 2.92) * mm});
            skLineSegment(sketch, "E8.6.0.54", {"start": v(-0.2, 3) * mm, "end": v(-0.2, 2.91) * mm});
            skLineSegment(sketch, "E8.9.0.54", {"start": v(0.2, 3) * mm, "end": v(-0.2, 3) * mm});
            skPoint(sketch, "E8.12.0.54", {"position": v(0, 2.96) * mm});
            skLineSegment(sketch, "E8.0.0.55", {"start": v(0.2, 3.24) * mm, "end": v(0.2, 3.15) * mm});
            skLineSegment(sketch, "E8.3.0.55", {"start": v(0.2, 3.16) * mm, "end": v(-0.2, 3.16) * mm});
            skLineSegment(sketch, "E8.6.0.55", {"start": v(-0.2, 3.24) * mm, "end": v(-0.2, 3.15) * mm});
            skLineSegment(sketch, "E8.9.0.55", {"start": v(0.2, 3.24) * mm, "end": v(-0.2, 3.24) * mm});
            skPoint(sketch, "E8.12.0.55", {"position": v(0, 3.2) * mm});
            skLineSegment(sketch, "E8.0.0.56", {"start": v(0.2, 3.48) * mm, "end": v(0.2, 3.4) * mm});
            skLineSegment(sketch, "E8.3.0.56", {"start": v(0.2, 3.4) * mm, "end": v(-0.2, 3.4) * mm});
            skLineSegment(sketch, "E8.6.0.56", {"start": v(-0.2, 3.48) * mm, "end": v(-0.2, 3.4) * mm});
            skLineSegment(sketch, "E8.9.0.56", {"start": v(0.2, 3.48) * mm, "end": v(-0.2, 3.48) * mm});
            skPoint(sketch, "E8.12.0.56", {"position": v(0, 3.44) * mm});
            skLineSegment(sketch, "E8.0.0.57", {"start": v(0.2, 3.72) * mm, "end": v(0.2, 3.63) * mm});
            skLineSegment(sketch, "E8.3.0.57", {"start": v(0.2, 3.63) * mm, "end": v(-0.2, 3.63) * mm});
            skLineSegment(sketch, "E8.6.0.57", {"start": v(-0.2, 3.72) * mm, "end": v(-0.2, 3.63) * mm});
            skLineSegment(sketch, "E8.9.0.57", {"start": v(0.2, 3.72) * mm, "end": v(-0.2, 3.72) * mm});
            skPoint(sketch, "E8.12.0.57", {"position": v(0, 3.68) * mm});
            skLineSegment(sketch, "E8.0.0.58", {"start": v(0.2, 3.96) * mm, "end": v(0.2, 3.87) * mm});
            skLineSegment(sketch, "E8.3.0.58", {"start": v(0.2, 3.88) * mm, "end": v(-0.2, 3.88) * mm});
            skLineSegment(sketch, "E8.6.0.58", {"start": v(-0.2, 3.96) * mm, "end": v(-0.2, 3.87) * mm});
            skLineSegment(sketch, "E8.9.0.58", {"start": v(0.2, 3.96) * mm, "end": v(-0.2, 3.96) * mm});
            skPoint(sketch, "E8.12.0.58", {"position": v(0, 3.92) * mm});
            skLineSegment(sketch, "E8.0.0.59", {"start": v(0.2, 4.2) * mm, "end": v(0.2, 4.11) * mm});
            skLineSegment(sketch, "E8.3.0.59", {"start": v(0.2, 4.12) * mm, "end": v(-0.2, 4.12) * mm});
            skLineSegment(sketch, "E8.6.0.59", {"start": v(-0.2, 4.2) * mm, "end": v(-0.2, 4.11) * mm});
            skLineSegment(sketch, "E8.9.0.59", {"start": v(0.2, 4.2) * mm, "end": v(-0.2, 4.2) * mm});
            skPoint(sketch, "E8.12.0.59", {"position": v(0, 4.16) * mm});
            skLineSegment(sketch, "E8.0.0.60", {"start": v(0.2, 4.44) * mm, "end": v(0.2, 4.35) * mm});
            skLineSegment(sketch, "E8.3.0.60", {"start": v(0.2, 4.35) * mm, "end": v(-0.2, 4.35) * mm});
            skLineSegment(sketch, "E8.6.0.60", {"start": v(-0.2, 4.44) * mm, "end": v(-0.2, 4.35) * mm});
            skLineSegment(sketch, "E8.9.0.60", {"start": v(0.2, 4.44) * mm, "end": v(-0.2, 4.44) * mm});
            skPoint(sketch, "E8.12.0.60", {"position": v(0, 4.4) * mm});
            skLineSegment(sketch, "E8.0.0.61", {"start": v(0.2, 4.68) * mm, "end": v(0.2, 4.6) * mm});
            skLineSegment(sketch, "E8.3.0.61", {"start": v(0.2, 4.6) * mm, "end": v(-0.2, 4.6) * mm});
            skLineSegment(sketch, "E8.6.0.61", {"start": v(-0.2, 4.68) * mm, "end": v(-0.2, 4.6) * mm});
            skLineSegment(sketch, "E8.9.0.61", {"start": v(0.2, 4.68) * mm, "end": v(-0.2, 4.68) * mm});
            skPoint(sketch, "E8.12.0.61", {"position": v(0, 4.64) * mm});
            skLineSegment(sketch, "E8.0.0.62", {"start": v(0.2, 4.92) * mm, "end": v(0.2, 4.83) * mm});
            skLineSegment(sketch, "E8.3.0.62", {"start": v(0.2, 4.83) * mm, "end": v(-0.2, 4.83) * mm});
            skLineSegment(sketch, "E8.6.0.62", {"start": v(-0.2, 4.92) * mm, "end": v(-0.2, 4.83) * mm});
            skLineSegment(sketch, "E8.9.0.62", {"start": v(0.2, 4.92) * mm, "end": v(-0.2, 4.92) * mm});
            skPoint(sketch, "E8.12.0.62", {"position": v(0, 4.88) * mm});
            skLineSegment(sketch, "E8.0.0.63", {"start": v(0.2, 5.16) * mm, "end": v(0.2, 5.07) * mm});
            skLineSegment(sketch, "E8.3.0.63", {"start": v(0.2, 5.07) * mm, "end": v(-0.2, 5.07) * mm});
            skLineSegment(sketch, "E8.6.0.63", {"start": v(-0.2, 5.16) * mm, "end": v(-0.2, 5.07) * mm});
            skLineSegment(sketch, "E8.9.0.63", {"start": v(0.2, 5.16) * mm, "end": v(-0.2, 5.16) * mm});
            skPoint(sketch, "E8.12.0.63", {"position": v(0, 5.12) * mm});
            skLineSegment(sketch, "E8.0.0.64", {"start": v(0.2, 5.4) * mm, "end": v(0.2, 5.31) * mm});
            skLineSegment(sketch, "E8.3.0.64", {"start": v(0.2, 5.32) * mm, "end": v(-0.2, 5.32) * mm});
            skLineSegment(sketch, "E8.6.0.64", {"start": v(-0.2, 5.4) * mm, "end": v(-0.2, 5.31) * mm});
            skLineSegment(sketch, "E8.9.0.64", {"start": v(0.2, 5.4) * mm, "end": v(-0.2, 5.4) * mm});
            skPoint(sketch, "E8.12.0.64", {"position": v(0, 5.36) * mm});
            skLineSegment(sketch, "E8.0.0.65", {"start": v(0.2, 5.64) * mm, "end": v(0.2, 5.55) * mm});
            skLineSegment(sketch, "E8.3.0.65", {"start": v(0.2, 5.56) * mm, "end": v(-0.2, 5.56) * mm});
            skLineSegment(sketch, "E8.6.0.65", {"start": v(-0.2, 5.64) * mm, "end": v(-0.2, 5.55) * mm});
            skLineSegment(sketch, "E8.9.0.65", {"start": v(0.2, 5.64) * mm, "end": v(-0.2, 5.64) * mm});
            skPoint(sketch, "E8.12.0.65", {"position": v(0, 5.6) * mm});
            skLineSegment(sketch, "E8.0.0.66", {"start": v(0.2, 5.88) * mm, "end": v(0.2, 5.8) * mm});
            skLineSegment(sketch, "E8.3.0.66", {"start": v(0.2, 5.8) * mm, "end": v(-0.2, 5.8) * mm});
            skLineSegment(sketch, "E8.6.0.66", {"start": v(-0.2, 5.88) * mm, "end": v(-0.2, 5.8) * mm});
            skLineSegment(sketch, "E8.9.0.66", {"start": v(0.2, 5.88) * mm, "end": v(-0.2, 5.88) * mm});
            skPoint(sketch, "E8.12.0.66", {"position": v(0, 5.84) * mm});
            skLineSegment(sketch, "E8.0.0.67", {"start": v(0.2, 6.12) * mm, "end": v(0.2, 6.03) * mm});
            skLineSegment(sketch, "E8.3.0.67", {"start": v(0.2, 6.03) * mm, "end": v(-0.2, 6.03) * mm});
            skLineSegment(sketch, "E8.6.0.67", {"start": v(-0.2, 6.12) * mm, "end": v(-0.2, 6.03) * mm});
            skLineSegment(sketch, "E8.9.0.67", {"start": v(0.2, 6.12) * mm, "end": v(-0.2, 6.12) * mm});
            skPoint(sketch, "E8.12.0.67", {"position": v(0, 6.08) * mm});
            skLineSegment(sketch, "E8.0.0.68", {"start": v(0.2, 6.36) * mm, "end": v(0.2, 6.27) * mm});
            skLineSegment(sketch, "E8.3.0.68", {"start": v(0.2, 6.28) * mm, "end": v(-0.2, 6.28) * mm});
            skLineSegment(sketch, "E8.6.0.68", {"start": v(-0.2, 6.36) * mm, "end": v(-0.2, 6.27) * mm});
            skLineSegment(sketch, "E8.9.0.68", {"start": v(0.2, 6.36) * mm, "end": v(-0.2, 6.36) * mm});
            skPoint(sketch, "E8.12.0.68", {"position": v(0, 6.32) * mm});
            skLineSegment(sketch, "E8.0.0.69", {"start": v(0.2, 6.6) * mm, "end": v(0.2, 6.51) * mm});
            skLineSegment(sketch, "E8.3.0.69", {"start": v(0.2, 6.51) * mm, "end": v(-0.2, 6.51) * mm});
            skLineSegment(sketch, "E8.6.0.69", {"start": v(-0.2, 6.6) * mm, "end": v(-0.2, 6.51) * mm});
            skLineSegment(sketch, "E8.9.0.69", {"start": v(0.2, 6.6) * mm, "end": v(-0.2, 6.6) * mm});
            skPoint(sketch, "E8.12.0.69", {"position": v(0, 6.56) * mm});
            skLineSegment(sketch, "E8.0.0.70", {"start": v(0.2, 6.84) * mm, "end": v(0.2, 6.75) * mm});
            skLineSegment(sketch, "E8.3.0.70", {"start": v(0.2, 6.75) * mm, "end": v(-0.2, 6.75) * mm});
            skLineSegment(sketch, "E8.6.0.70", {"start": v(-0.2, 6.84) * mm, "end": v(-0.2, 6.75) * mm});
            skLineSegment(sketch, "E8.9.0.70", {"start": v(0.2, 6.84) * mm, "end": v(-0.2, 6.84) * mm});
            skPoint(sketch, "E8.12.0.70", {"position": v(0, 6.8) * mm});
            skLineSegment(sketch, "E8.0.0.71", {"start": v(0.2, 7.08) * mm, "end": v(0.2, 7) * mm});
            skLineSegment(sketch, "E8.3.0.71", {"start": v(0.2, 7) * mm, "end": v(-0.2, 7) * mm});
            skLineSegment(sketch, "E8.6.0.71", {"start": v(-0.2, 7.08) * mm, "end": v(-0.2, 7) * mm});
            skLineSegment(sketch, "E8.9.0.71", {"start": v(0.2, 7.08) * mm, "end": v(-0.2, 7.08) * mm});
            skPoint(sketch, "E8.12.0.71", {"position": v(0, 7.04) * mm});
            skLineSegment(sketch, "E8.0.0.72", {"start": v(0.2, 7.32) * mm, "end": v(0.2, 7.23) * mm});
            skLineSegment(sketch, "E8.3.0.72", {"start": v(0.2, 7.23) * mm, "end": v(-0.2, 7.23) * mm});
            skLineSegment(sketch, "E8.6.0.72", {"start": v(-0.2, 7.32) * mm, "end": v(-0.2, 7.23) * mm});
            skLineSegment(sketch, "E8.9.0.72", {"start": v(0.2, 7.32) * mm, "end": v(-0.2, 7.32) * mm});
            skPoint(sketch, "E8.12.0.72", {"position": v(0, 7.28) * mm});
            skLineSegment(sketch, "E8.0.0.73", {"start": v(0.2, 7.56) * mm, "end": v(0.2, 7.47) * mm});
            skLineSegment(sketch, "E8.3.0.73", {"start": v(0.2, 7.47) * mm, "end": v(-0.2, 7.47) * mm});
            skLineSegment(sketch, "E8.6.0.73", {"start": v(-0.2, 7.56) * mm, "end": v(-0.2, 7.47) * mm});
            skLineSegment(sketch, "E8.9.0.73", {"start": v(0.2, 7.56) * mm, "end": v(-0.2, 7.56) * mm});
            skPoint(sketch, "E8.12.0.73", {"position": v(0, 7.52) * mm});
            skLineSegment(sketch, "E8.0.0.74", {"start": v(0.2, 7.8) * mm, "end": v(0.2, 7.71) * mm});
            skLineSegment(sketch, "E8.3.0.74", {"start": v(0.2, 7.71) * mm, "end": v(-0.2, 7.71) * mm});
            skLineSegment(sketch, "E8.6.0.74", {"start": v(-0.2, 7.8) * mm, "end": v(-0.2, 7.71) * mm});
            skLineSegment(sketch, "E8.9.0.74", {"start": v(0.2, 7.8) * mm, "end": v(-0.2, 7.8) * mm});
            skPoint(sketch, "E8.12.0.74", {"position": v(0, 7.76) * mm});
            skLineSegment(sketch, "E8.0.0.75", {"start": v(0.2, 8.04) * mm, "end": v(0.2, 7.95) * mm});
            skLineSegment(sketch, "E8.3.0.75", {"start": v(0.2, 7.95) * mm, "end": v(-0.2, 7.95) * mm});
            skLineSegment(sketch, "E8.6.0.75", {"start": v(-0.2, 8.04) * mm, "end": v(-0.2, 7.95) * mm});
            skLineSegment(sketch, "E8.9.0.75", {"start": v(0.2, 8.04) * mm, "end": v(-0.2, 8.04) * mm});
            skPoint(sketch, "E8.12.0.75", {"position": v(0, 8) * mm});
            skLineSegment(sketch, "E8.0.0.76", {"start": v(0.2, 8.28) * mm, "end": v(0.2, 8.2) * mm});
            skLineSegment(sketch, "E8.3.0.76", {"start": v(0.2, 8.2) * mm, "end": v(-0.2, 8.2) * mm});
            skLineSegment(sketch, "E8.6.0.76", {"start": v(-0.2, 8.28) * mm, "end": v(-0.2, 8.2) * mm});
            skLineSegment(sketch, "E8.9.0.76", {"start": v(0.2, 8.28) * mm, "end": v(-0.2, 8.28) * mm});
            skPoint(sketch, "E8.12.0.76", {"position": v(0, 8.24) * mm});
            skLineSegment(sketch, "E8.0.0.77", {"start": v(0.2, 8.52) * mm, "end": v(0.2, 8.43) * mm});
            skLineSegment(sketch, "E8.3.0.77", {"start": v(0.2, 8.43) * mm, "end": v(-0.2, 8.43) * mm});
            skLineSegment(sketch, "E8.6.0.77", {"start": v(-0.2, 8.52) * mm, "end": v(-0.2, 8.43) * mm});
            skLineSegment(sketch, "E8.9.0.77", {"start": v(0.2, 8.52) * mm, "end": v(-0.2, 8.52) * mm});
            skPoint(sketch, "E8.12.0.77", {"position": v(0, 8.48) * mm});
            skLineSegment(sketch, "E8.0.0.78", {"start": v(0.2, 8.76) * mm, "end": v(0.2, 8.67) * mm});
            skLineSegment(sketch, "E8.3.0.78", {"start": v(0.2, 8.67) * mm, "end": v(-0.2, 8.67) * mm});
            skLineSegment(sketch, "E8.6.0.78", {"start": v(-0.2, 8.76) * mm, "end": v(-0.2, 8.67) * mm});
            skLineSegment(sketch, "E8.9.0.78", {"start": v(0.2, 8.76) * mm, "end": v(-0.2, 8.76) * mm});
            skPoint(sketch, "E8.12.0.78", {"position": v(0, 8.72) * mm});
            skLineSegment(sketch, "E8.0.0.79", {"start": v(0.2, 9) * mm, "end": v(0.2, 8.91) * mm});
            skLineSegment(sketch, "E8.3.0.79", {"start": v(0.2, 8.91) * mm, "end": v(-0.2, 8.91) * mm});
            skLineSegment(sketch, "E8.6.0.79", {"start": v(-0.2, 9) * mm, "end": v(-0.2, 8.91) * mm});
            skLineSegment(sketch, "E8.9.0.79", {"start": v(0.2, 9) * mm, "end": v(-0.2, 9) * mm});
            skPoint(sketch, "E8.12.0.79", {"position": v(0, 8.96) * mm});
            skLineSegment(sketch, "E8.0.0.80", {"start": v(0.2, 9.24) * mm, "end": v(0.2, 9.15) * mm});
            skLineSegment(sketch, "E8.3.0.80", {"start": v(0.2, 9.15) * mm, "end": v(-0.2, 9.15) * mm});
            skLineSegment(sketch, "E8.6.0.80", {"start": v(-0.2, 9.24) * mm, "end": v(-0.2, 9.15) * mm});
            skLineSegment(sketch, "E8.9.0.80", {"start": v(0.2, 9.24) * mm, "end": v(-0.2, 9.24) * mm});
            skPoint(sketch, "E8.12.0.80", {"position": v(0, 9.2) * mm});
            skLineSegment(sketch, "E8.0.0.81", {"start": v(0.2, 9.48) * mm, "end": v(0.2, 9.4) * mm});
            skLineSegment(sketch, "E8.3.0.81", {"start": v(0.2, 9.4) * mm, "end": v(-0.2, 9.4) * mm});
            skLineSegment(sketch, "E8.6.0.81", {"start": v(-0.2, 9.48) * mm, "end": v(-0.2, 9.4) * mm});
            skLineSegment(sketch, "E8.9.0.81", {"start": v(0.2, 9.48) * mm, "end": v(-0.2, 9.48) * mm});
            skPoint(sketch, "E8.12.0.81", {"position": v(0, 9.44) * mm});
            skLineSegment(sketch, "E8.0.0.82", {"start": v(0.2, 9.72) * mm, "end": v(0.2, 9.63) * mm});
            skLineSegment(sketch, "E8.3.0.82", {"start": v(0.2, 9.63) * mm, "end": v(-0.2, 9.63) * mm});
            skLineSegment(sketch, "E8.6.0.82", {"start": v(-0.2, 9.72) * mm, "end": v(-0.2, 9.63) * mm});
            skLineSegment(sketch, "E8.9.0.82", {"start": v(0.2, 9.72) * mm, "end": v(-0.2, 9.72) * mm});
            skPoint(sketch, "E8.12.0.82", {"position": v(0, 9.68) * mm});
            skLineSegment(sketch, "E8.0.0.83", {"start": v(0.2, 9.96) * mm, "end": v(0.2, 9.87) * mm});
            skLineSegment(sketch, "E8.3.0.83", {"start": v(0.2, 9.87) * mm, "end": v(-0.2, 9.87) * mm});
            skLineSegment(sketch, "E8.6.0.83", {"start": v(-0.2, 9.96) * mm, "end": v(-0.2, 9.87) * mm});
            skLineSegment(sketch, "E8.9.0.83", {"start": v(0.2, 9.96) * mm, "end": v(-0.2, 9.96) * mm});
            skPoint(sketch, "E8.12.0.83", {"position": v(0, 9.92) * mm});
            skLineSegment(sketch, "E8.0.0.84", {"start": v(0.2, 10.2) * mm, "end": v(0.2, 10.11) * mm});
            skLineSegment(sketch, "E8.3.0.84", {"start": v(0.2, 10.11) * mm, "end": v(-0.2, 10.11) * mm});
            skLineSegment(sketch, "E8.6.0.84", {"start": v(-0.2, 10.2) * mm, "end": v(-0.2, 10.11) * mm});
            skLineSegment(sketch, "E8.9.0.84", {"start": v(0.2, 10.2) * mm, "end": v(-0.2, 10.2) * mm});
            skPoint(sketch, "E8.12.0.84", {"position": v(0, 10.16) * mm});
            skLineSegment(sketch, "E8.0.0.85", {"start": v(0.2, 10.44) * mm, "end": v(0.2, 10.35) * mm});
            skLineSegment(sketch, "E8.3.0.85", {"start": v(0.2, 10.35) * mm, "end": v(-0.2, 10.35) * mm});
            skLineSegment(sketch, "E8.6.0.85", {"start": v(-0.2, 10.44) * mm, "end": v(-0.2, 10.35) * mm});
            skLineSegment(sketch, "E8.9.0.85", {"start": v(0.2, 10.44) * mm, "end": v(-0.2, 10.44) * mm});
            skPoint(sketch, "E8.12.0.85", {"position": v(0, 10.4) * mm});
            skLineSegment(sketch, "E8.0.0.86", {"start": v(0.2, 10.68) * mm, "end": v(0.2, 10.6) * mm});
            skLineSegment(sketch, "E8.3.0.86", {"start": v(0.2, 10.6) * mm, "end": v(-0.2, 10.6) * mm});
            skLineSegment(sketch, "E8.6.0.86", {"start": v(-0.2, 10.68) * mm, "end": v(-0.2, 10.6) * mm});
            skLineSegment(sketch, "E8.9.0.86", {"start": v(0.2, 10.68) * mm, "end": v(-0.2, 10.68) * mm});
            skPoint(sketch, "E8.12.0.86", {"position": v(0, 10.64) * mm});
            skLineSegment(sketch, "E8.0.0.87", {"start": v(0.2, 10.92) * mm, "end": v(0.2, 10.83) * mm});
            skLineSegment(sketch, "E8.3.0.87", {"start": v(0.2, 10.83) * mm, "end": v(-0.2, 10.83) * mm});
            skLineSegment(sketch, "E8.6.0.87", {"start": v(-0.2, 10.92) * mm, "end": v(-0.2, 10.83) * mm});
            skLineSegment(sketch, "E8.9.0.87", {"start": v(0.2, 10.92) * mm, "end": v(-0.2, 10.92) * mm});
            skPoint(sketch, "E8.12.0.87", {"position": v(0, 10.88) * mm});
            skLineSegment(sketch, "E8.0.0.88", {"start": v(0.2, 11.16) * mm, "end": v(0.2, 11.07) * mm});
            skLineSegment(sketch, "E8.3.0.88", {"start": v(0.2, 11.07) * mm, "end": v(-0.2, 11.07) * mm});
            skLineSegment(sketch, "E8.6.0.88", {"start": v(-0.2, 11.16) * mm, "end": v(-0.2, 11.07) * mm});
            skLineSegment(sketch, "E8.9.0.88", {"start": v(0.2, 11.16) * mm, "end": v(-0.2, 11.16) * mm});
            skPoint(sketch, "E8.12.0.88", {"position": v(0, 11.12) * mm});
            skLineSegment(sketch, "E8.0.0.89", {"start": v(0.2, 11.4) * mm, "end": v(0.2, 11.31) * mm});
            skLineSegment(sketch, "E8.3.0.89", {"start": v(0.2, 11.31) * mm, "end": v(-0.2, 11.31) * mm});
            skLineSegment(sketch, "E8.6.0.89", {"start": v(-0.2, 11.4) * mm, "end": v(-0.2, 11.31) * mm});
            skLineSegment(sketch, "E8.9.0.89", {"start": v(0.2, 11.4) * mm, "end": v(-0.2, 11.4) * mm});
            skPoint(sketch, "E8.12.0.89", {"position": v(0, 11.36) * mm});
            skLineSegment(sketch, "E8.0.0.90", {"start": v(0.2, 11.64) * mm, "end": v(0.2, 11.55) * mm});
            skLineSegment(sketch, "E8.3.0.90", {"start": v(0.2, 11.55) * mm, "end": v(-0.2, 11.55) * mm});
            skLineSegment(sketch, "E8.6.0.90", {"start": v(-0.2, 11.64) * mm, "end": v(-0.2, 11.55) * mm});
            skLineSegment(sketch, "E8.9.0.90", {"start": v(0.2, 11.64) * mm, "end": v(-0.2, 11.64) * mm});
            skPoint(sketch, "E8.12.0.90", {"position": v(0, 11.6) * mm});
            skLineSegment(sketch, "E8.0.0.91", {"start": v(0.2, 11.88) * mm, "end": v(0.2, 11.8) * mm});
            skLineSegment(sketch, "E8.3.0.91", {"start": v(0.2, 11.8) * mm, "end": v(-0.2, 11.8) * mm});
            skLineSegment(sketch, "E8.6.0.91", {"start": v(-0.2, 11.88) * mm, "end": v(-0.2, 11.8) * mm});
            skLineSegment(sketch, "E8.9.0.91", {"start": v(0.2, 11.88) * mm, "end": v(-0.2, 11.88) * mm});
            skPoint(sketch, "E8.12.0.91", {"position": v(0, 11.84) * mm});
            skLineSegment(sketch, "E8.0.0.92", {"start": v(0.2, 12.12) * mm, "end": v(0.2, 12.03) * mm});
            skLineSegment(sketch, "E8.3.0.92", {"start": v(0.2, 12.03) * mm, "end": v(-0.2, 12.03) * mm});
            skLineSegment(sketch, "E8.6.0.92", {"start": v(-0.2, 12.12) * mm, "end": v(-0.2, 12.03) * mm});
            skLineSegment(sketch, "E8.9.0.92", {"start": v(0.2, 12.12) * mm, "end": v(-0.2, 12.12) * mm});
            skPoint(sketch, "E8.12.0.92", {"position": v(0, 12.08) * mm});
            skLineSegment(sketch, "E8.0.0.93", {"start": v(0.2, 12.36) * mm, "end": v(0.2, 12.27) * mm});
            skLineSegment(sketch, "E8.3.0.93", {"start": v(0.2, 12.27) * mm, "end": v(-0.2, 12.27) * mm});
            skLineSegment(sketch, "E8.6.0.93", {"start": v(-0.2, 12.36) * mm, "end": v(-0.2, 12.27) * mm});
            skLineSegment(sketch, "E8.9.0.93", {"start": v(0.2, 12.36) * mm, "end": v(-0.2, 12.36) * mm});
            skPoint(sketch, "E8.12.0.93", {"position": v(0, 12.32) * mm});
            skLineSegment(sketch, "E8.0.0.94", {"start": v(0.2, 12.6) * mm, "end": v(0.2, 12.51) * mm});
            skLineSegment(sketch, "E8.3.0.94", {"start": v(0.2, 12.51) * mm, "end": v(-0.2, 12.51) * mm});
            skLineSegment(sketch, "E8.6.0.94", {"start": v(-0.2, 12.6) * mm, "end": v(-0.2, 12.51) * mm});
            skLineSegment(sketch, "E8.9.0.94", {"start": v(0.2, 12.6) * mm, "end": v(-0.2, 12.6) * mm});
            skPoint(sketch, "E8.12.0.94", {"position": v(0, 12.56) * mm});
            skLineSegment(sketch, "E8.0.0.95", {"start": v(0.2, 12.84) * mm, "end": v(0.2, 12.75) * mm});
            skLineSegment(sketch, "E8.3.0.95", {"start": v(0.2, 12.75) * mm, "end": v(-0.2, 12.75) * mm});
            skLineSegment(sketch, "E8.6.0.95", {"start": v(-0.2, 12.84) * mm, "end": v(-0.2, 12.75) * mm});
            skLineSegment(sketch, "E8.9.0.95", {"start": v(0.2, 12.84) * mm, "end": v(-0.2, 12.84) * mm});
            skPoint(sketch, "E8.12.0.95", {"position": v(0, 12.8) * mm});
            skLineSegment(sketch, "E8.0.0.96", {"start": v(0.2, 13.08) * mm, "end": v(0.2, 13) * mm});
            skLineSegment(sketch, "E8.3.0.96", {"start": v(0.2, 13) * mm, "end": v(-0.2, 13) * mm});
            skLineSegment(sketch, "E8.6.0.96", {"start": v(-0.2, 13.08) * mm, "end": v(-0.2, 13) * mm});
            skLineSegment(sketch, "E8.9.0.96", {"start": v(0.2, 13.08) * mm, "end": v(-0.2, 13.08) * mm});
            skPoint(sketch, "E8.12.0.96", {"position": v(0, 13.04) * mm});
            skLineSegment(sketch, "E8.0.0.97", {"start": v(0.2, 13.32) * mm, "end": v(0.2, 13.23) * mm});
            skLineSegment(sketch, "E8.3.0.97", {"start": v(0.2, 13.23) * mm, "end": v(-0.2, 13.23) * mm});
            skLineSegment(sketch, "E8.6.0.97", {"start": v(-0.2, 13.32) * mm, "end": v(-0.2, 13.23) * mm});
            skLineSegment(sketch, "E8.9.0.97", {"start": v(0.2, 13.32) * mm, "end": v(-0.2, 13.32) * mm});
            skPoint(sketch, "E8.12.0.97", {"position": v(0, 13.28) * mm});
            skLineSegment(sketch, "E8.0.0.98", {"start": v(0.2, 13.56) * mm, "end": v(0.2, 13.47) * mm});
            skLineSegment(sketch, "E8.3.0.98", {"start": v(0.2, 13.47) * mm, "end": v(-0.2, 13.47) * mm});
            skLineSegment(sketch, "E8.6.0.98", {"start": v(-0.2, 13.56) * mm, "end": v(-0.2, 13.47) * mm});
            skLineSegment(sketch, "E8.9.0.98", {"start": v(0.2, 13.56) * mm, "end": v(-0.2, 13.56) * mm});
            skPoint(sketch, "E8.12.0.98", {"position": v(0, 13.52) * mm});
            skLineSegment(sketch, "E8.0.0.99", {"start": v(0.2, 13.8) * mm, "end": v(0.2, 13.71) * mm});
            skLineSegment(sketch, "E8.3.0.99", {"start": v(0.2, 13.71) * mm, "end": v(-0.2, 13.71) * mm});
            skLineSegment(sketch, "E8.6.0.99", {"start": v(-0.2, 13.8) * mm, "end": v(-0.2, 13.71) * mm});
            skLineSegment(sketch, "E8.9.0.99", {"start": v(0.2, 13.8) * mm, "end": v(-0.2, 13.8) * mm});
            skPoint(sketch, "E8.12.0.99", {"position": v(0, 13.76) * mm});
            skSolve(sketch);
        }
        {
            var Q0;
            Q0 = qSketchRegion(id + "F12", true);
            extrude(context, id + "F13", {"entities" : qUnion([Q0]), "operationType" : NewBodyOperationType.REMOVE, "oppositeDirection" : true, "depth" : (getVariable(context, 'detch') + getVariable(context, 'tox')) * mm});
        }
        {
            var Q0;
            Q0 = qSketchRegion(id + "F2", true);
            extrude(context, id + "F14", {"entities" : qUnion([Q0]), "depth" : getVariable(context, 'Lz') / 2, "offsetDistance" : 25 * mm, "hasSecondDirection" : true, "secondDirectionOppositeDirection" : true, "secondDirectionDepth" : getVariable(context, 'Lz') / 2});
        }
    });
